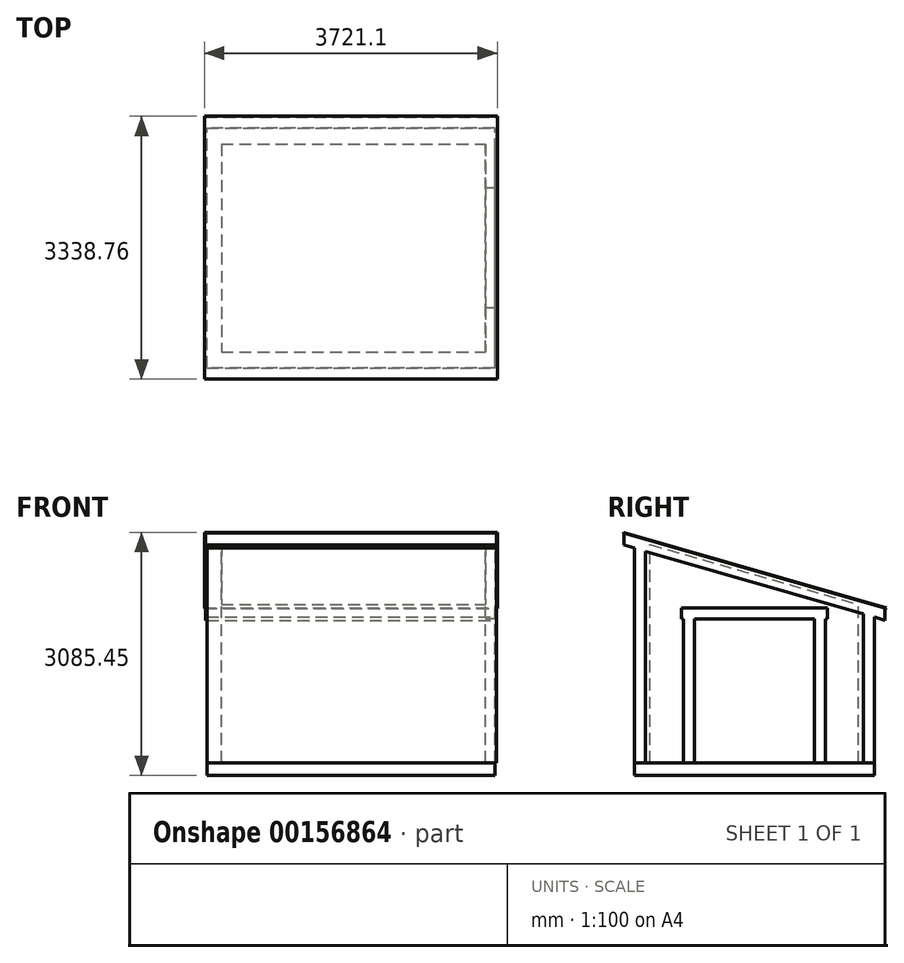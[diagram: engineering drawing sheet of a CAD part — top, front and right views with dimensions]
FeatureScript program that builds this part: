
annotation { "Feature Type Name" : "Feature", "Feature Type Description" : "" }
export const myFeature = defineFeature(function(context is Context, id is Id, definition is map)
    precondition{}
    {
        {
            var Q0;
            Q0=qCreatedBy(makeId("Top.planeOp"),FACE);
            var sketch = newSketch(context, id + "F0", { "sketchPlane" : qUnion([Q0])});
            skLineSegment(sketch, "E0.bottom", {"start": v(-3657.6, 0) * mm, "end": v(0, 0) * mm});
            skLineSegment(sketch, "E0.top", {"start": v(-3657.6, 3048) * mm, "end": v(0, 3048) * mm});
            skLineSegment(sketch, "E0.left", {"start": v(0, 0) * mm, "end": v(0, 3048) * mm});
            skLineSegment(sketch, "E0.right", {"start": v(-3657.6, 0) * mm, "end": v(-3657.6, 3048) * mm});
            skSolve(sketch);
        }
        {
            var Q0;
            Q0=makeQuery(id+"F0.imprint","IMPRINT",FACE,{"disambiguationData":[TD([[makeQuery(id+"F0.imprint","IMPRINT",EDGE,{"derivedFrom":sQuery(id+"F0.wireOp",EDGE,"E0.bottom")}),1.0]])]});
            extrude(context, id + "F1", {"entities" : qUnion([Q0]), "depth" : 2880.36 * mm});
        }
        {
            var Q0;
            Q0=makeQuery(id+"F1.opExtrude","CAP_EDGE",EDGE,{"disambiguationData":[OSD([sQuery(id+"F0.wireOp",EDGE,"E0.top")])],"isStart":false});
            chamfer(context, id + "F2", {"entities" : qUnion([Q0]), "chamferType" : ChamferType.TWO_OFFSETS, "width1" : 876.3 * mm, "oppositeDirection" : false, "width2" : 3048 * mm, "tangentPropagation" : true});
        }
        {
            var Q0;
            Q0=makeQuery(id+"F2.opChamfer","BLEND_FACE",FACE,{"disambiguationData":[OSD([sQuery(id+"F0.wireOp",EDGE,"E0.top")])]});
            var sketch = newSketch(context, id + "F3", { "sketchPlane" : qUnion([Q0])});
            skLineSegment(sketch, "E1.1", {"start": v(-3676.65, -937.33) * mm, "end": v(-3676.65, 2517.07) * mm});
            skLineSegment(sketch, "E1.3", {"start": v(19.05, 2517.07) * mm, "end": v(19.05, -937.33) * mm});
            skLineSegment(sketch, "E2", {"start": v(19.05, 789.87) * mm, "end": v(0, 789.87) * mm, "construction": true});
            skLineSegment(sketch, "E3", {"start": v(0, 789.87) * mm, "end": v(-3657.6, 789.87) * mm, "construction": true});
            skLineSegment(sketch, "E4.0", {"start": v(-3657.6, -795.86) * mm, "end": v(-3657.6, 743.55) * mm, "construction": true});
            skLineSegment(sketch, "E5", {"start": v(-3657.6, 789.87) * mm, "end": v(-3657.6, 2375.6) * mm, "construction": true});
            skLineSegment(sketch, "E6", {"start": v(-3657.6, 743.55) * mm, "end": v(-3657.6, 789.87) * mm, "construction": true});
            skLineSegment(sketch, "E7", {"start": v(-3657.6, 789.87) * mm, "end": v(-3676.65, 789.87) * mm, "construction": true});
            skLineSegment(sketch, "E8", {"start": v(19.05, -937.33) * mm, "end": v(-3676.65, -937.33) * mm});
            skLineSegment(sketch, "E9", {"start": v(-3676.65, 2517.07) * mm, "end": v(19.05, 2517.07) * mm});
            skLineSegment(sketch, "E10.0", {"start": v(-3657.6, -795.86) * mm, "end": v(0, -795.86) * mm, "construction": true});
            skLineSegment(sketch, "E10.1", {"start": v(0, 2375.6) * mm, "end": v(0, -795.86) * mm, "construction": true});
            skSolve(sketch);
        }
        {
            var Q0;
            Q0=makeQuery(id+"F1.opExtrude","SWEPT_FACE",FACE,{"disambiguationData":[OSD([sQuery(id+"F0.wireOp",EDGE,"E0.left")])]});
            var sketch = newSketch(context, id + "F4", { "sketchPlane" : qUnion([Q0])});
            skLineSegment(sketch, "E11.0", {"start": v(0, 2880.36) * mm, "end": v(0, 0) * mm, "construction": true});
            skLineSegment(sketch, "E12", {"start": v(0, 2880.36) * mm, "end": v(0, 2727.96) * mm});
            skSolve(sketch);
        }
        {
            var Q0;
            Q0=makeQuery(id+"F3.imprint","IMPRINT",FACE,{"disambiguationData":[TD([[makeQuery(id+"F3.imprint","IMPRINT",EDGE,{"derivedFrom":sQuery(id+"F3.wireOp",EDGE,"E1.1")}),-1.0]])]});
            var Q1;
            Q1=sQuery(id+"F4.wireOp",EDGE,"E12");
            sweep(context, id + "F5", {"operationType" : NewBodyOperationType.ADD, "profiles" : qUnion([Q0]), "path" : qUnion([Q1])});
        }
        {
            var Q0;
            {var subQ0=sQuery(id+"F0.wireOp",EDGE,"E0.top");Q0=makeQuery(id+"F5.boolean.opBoolean","MERGE",FACE,{"derivedFrom":[makeQuery(id+"F2.opChamfer","BLEND_FACE",FACE,{"disambiguationData":[OSD([subQ0])]}),makeQuery(id+"F5.opSweep","CAP_FACE",FACE,{"disambiguationData":[OSD([sQuery(id+"F0.wireOp",EDGE,"E0.bottom"),subQ0,sQuery(id+"F0.wireOp",EDGE,"E0.left"),sQuery(id+"F0.wireOp",EDGE,"E0.right"),sQuery(id+"F3.wireOp",EDGE,"E1.1"),sQuery(id+"F3.wireOp",EDGE,"E1.3"),sQuery(id+"F3.wireOp",EDGE,"E8"),sQuery(id+"F3.wireOp",EDGE,"E9"),sQuery(id+"F4.wireOp",VERTEX,"E12.start")])],"isStart":true})]});}
            var sketch = newSketch(context, id + "F6", { "sketchPlane" : qUnion([Q0])});
            skLineSegment(sketch, "E13.0", {"start": v(19.05, -937.33) * mm, "end": v(-3676.65, -937.33) * mm, "construction": true});
            skLineSegment(sketch, "E13.1", {"start": v(19.05, 2517.07) * mm, "end": v(19.05, -937.33) * mm, "construction": true});
            skLineSegment(sketch, "E13.2", {"start": v(-3676.65, 2517.07) * mm, "end": v(19.05, 2517.07) * mm, "construction": true});
            skLineSegment(sketch, "E13.3", {"start": v(-3676.65, -895.22) * mm, "end": v(-3676.65, 2559.18) * mm, "construction": true});
            skLineSegment(sketch, "E14", {"start": v(31.75, -942.41) * mm, "end": v(-3689.35, -942.41) * mm});
            skLineSegment(sketch, "E15", {"start": v(-3689.35, -942.41) * mm, "end": v(-3689.35, 2529.77) * mm});
            skLineSegment(sketch, "E16", {"start": v(-3689.35, 2529.77) * mm, "end": v(31.75, 2529.77) * mm});
            skLineSegment(sketch, "E17", {"start": v(31.75, 2529.77) * mm, "end": v(31.75, -942.41) * mm});
            skLineSegment(sketch, "E18", {"start": v(-461.3, -942.41) * mm, "end": v(-461.3, -937.33) * mm, "construction": true});
            skLineSegment(sketch, "E19", {"start": v(-683.5, 2517.07) * mm, "end": v(-683.5, 2529.77) * mm, "construction": true});
            skLineSegment(sketch, "E20", {"start": v(31.75, 1297.2) * mm, "end": v(19.05, 1297.2) * mm, "construction": true});
            skLineSegment(sketch, "E21", {"start": v(-3676.65, 831.98) * mm, "end": v(-3689.35, 831.98) * mm, "construction": true});
            skPoint(sketch, "E21.endSnap0", {"position": v(-3689.35, 793.68) * mm});
            skSolve(sketch);
        }
        {
            var Q0;
            Q0 = qSketchRegion(id + "F6", true);
            extrude(context, id + "F7", {"entities" : qUnion([Q0]), "operationType" : NewBodyOperationType.ADD, "depth" : 6.35 * mm});
        }
        {
            var Q0;
            Q0=makeQuery(id+"F1.opExtrude","SWEPT_FACE",FACE,{"disambiguationData":[OSD([sQuery(id+"F0.wireOp",EDGE,"E0.left")])]});
            var sketch = newSketch(context, id + "F8", { "sketchPlane" : qUnion([Q0])});
            skLineSegment(sketch, "E22.top", {"start": v(0, 0) * mm, "end": v(139.7, 0) * mm});
            skLineSegment(sketch, "E22.left", {"start": v(0, 2727.96) * mm, "end": v(0, 0) * mm});
            skLineSegment(sketch, "E22.right", {"start": v(139.7, 2687.8) * mm, "end": v(139.7, 0) * mm});
            skLineSegment(sketch, "E23", {"start": v(0, 2727.96) * mm, "end": v(139.7, 2687.8) * mm});
            skLineSegment(sketch, "E24.bottom", {"start": v(3048, 0) * mm, "end": v(2908.3, 0) * mm});
            skLineSegment(sketch, "E24.left", {"start": v(3048, 0) * mm, "end": v(3048, 1851.66) * mm});
            skLineSegment(sketch, "E24.right", {"start": v(2908.3, 0) * mm, "end": v(2908.3, 1891.82) * mm});
            skLineSegment(sketch, "E25", {"start": v(2908.3, 1891.82) * mm, "end": v(3048, 1851.66) * mm});
            skLineSegment(sketch, "E26", {"start": v(139.7, 0) * mm, "end": v(2908.3, 0) * mm, "construction": true});
            skLineSegment(sketch, "E27.bottom", {"start": v(2286, 1828.8) * mm, "end": v(762, 1828.8) * mm, "construction": true});
            skLineSegment(sketch, "E27.left", {"start": v(2286, 1828.8) * mm, "end": v(2286, 0) * mm, "construction": true});
            skLineSegment(sketch, "E27.right", {"start": v(762, 1828.8) * mm, "end": v(762, 0) * mm, "construction": true});
            skPoint(sketch, "E27.middle", {"position": v(1524, 0) * mm});
            skPoint(sketch, "E28", {"position": v(1524, 1828.8) * mm});
            skLineSegment(sketch, "E29", {"start": v(1524, 1828.8) * mm, "end": v(1524, 0) * mm, "construction": true});
            skLineSegment(sketch, "E30.bottom", {"start": v(762, 0) * mm, "end": v(622.3, 0) * mm});
            skLineSegment(sketch, "E30.top", {"start": v(762, 1828.8) * mm, "end": v(622.3, 1828.8) * mm});
            skLineSegment(sketch, "E30.left", {"start": v(762, 0) * mm, "end": v(762, 1828.8) * mm});
            skLineSegment(sketch, "E30.right", {"start": v(622.3, 0) * mm, "end": v(622.3, 1828.8) * mm});
            skLineSegment(sketch, "E31.MirrorCS", {"start": v(2425.7, 0) * mm, "end": v(2425.7, 1828.8) * mm});
            skLineSegment(sketch, "E32.MirrorCS", {"start": v(2286, 1828.8) * mm, "end": v(2425.7, 1828.8) * mm});
            skLineSegment(sketch, "E33.MirrorCS", {"start": v(2908.3, 0) * mm, "end": v(139.7, 0) * mm, "construction": true});
            skLineSegment(sketch, "E34", {"start": v(2286, 1828.8) * mm, "end": v(2286, 0) * mm});
            skLineSegment(sketch, "E35", {"start": v(1524, 1828.8) * mm, "end": v(2451.1, 1828.8) * mm});
            skLineSegment(sketch, "E36", {"start": v(2451.1, 1828.8) * mm, "end": v(2451.1, 1968.5) * mm});
            skLineSegment(sketch, "E37", {"start": v(2451.1, 1968.5) * mm, "end": v(1524, 1968.5) * mm});
            skLineSegment(sketch, "E38.MirrorCS", {"start": v(596.9, 1968.5) * mm, "end": v(1524, 1968.5) * mm});
            skLineSegment(sketch, "E39.MirrorCS", {"start": v(596.9, 1828.8) * mm, "end": v(596.9, 1968.5) * mm});
            skLineSegment(sketch, "E40.MirrorCS", {"start": v(1524, 1828.8) * mm, "end": v(596.9, 1828.8) * mm});
            skLineSegment(sketch, "E41", {"start": v(2286, 0) * mm, "end": v(2425.7, 0) * mm});
            skSolve(sketch);
        }
        {
            var Q0;
            Q0 = qSketchRegion(id + "F8", true);
            extrude(context, id + "F9", {"entities" : qUnion([Q0]), "operationType" : NewBodyOperationType.ADD, "depth" : 19.05 * mm});
        }
        {
            var Q0;
            {var subQ0=sQuery(id+"F0.wireOp",EDGE,"E0.left");Q0=makeQuery(id+"F9.boolean.opBoolean","SPLIT",FACE,{"disambiguationData":[TD([makeQuery(id+"F9.opExtrude","SWEPT_FACE",FACE,{"disambiguationData":[OSD([sQuery(id+"F8.wireOp",EDGE,"E30.left")])]})])],"derivedFrom":makeQuery(id+"F1.opExtrude","SWEPT_FACE",FACE,{"disambiguationData":[OSD([subQ0])]})});}
            extrude(context, id + "F10", {"entities" : qUnion([Q0]), "operationType" : NewBodyOperationType.REMOVE, "oppositeDirection" : true, "depth" : 121.92 * mm});
        }
        {
            var Q0;
            Q0=makeQuery(id+"F10.boolean.opBoolean","COPY",FACE,{"derivedFrom":makeQuery(id+"F10.opExtrude","CAP_FACE",FACE,{"disambiguationData":[OSD([sQuery(id+"F0.wireOp",EDGE,"E0.left")])],"isStart":false})});
            var sketch = newSketch(context, id + "F11", { "sketchPlane" : qUnion([Q0])});
            skLineSegment(sketch, "E42.bottom", {"start": v(2843.33, 0) * mm, "end": v(198.9, 0) * mm});
            skLineSegment(sketch, "E42.left", {"start": v(2843.33, 0) * mm, "end": v(2843.33, 2012.4) * mm});
            skLineSegment(sketch, "E42.right", {"start": v(198.9, 0) * mm, "end": v(198.9, 2772.67) * mm});
            skLineSegment(sketch, "E43", {"start": v(198.9, 2772.67) * mm, "end": v(2843.33, 2012.4) * mm});
            skSolve(sketch);
        }
        {
            var Q0;
            Q0 = qSketchRegion(id + "F11", true);
            extrude(context, id + "F12", {"entities" : qUnion([Q0]), "operationType" : NewBodyOperationType.REMOVE, "oppositeDirection" : true, "depth" : 3352.8 * mm});
        }
        {
            var Q0;
            Q0=qCreatedBy(makeId("Top.planeOp"),FACE);
            var sketch = newSketch(context, id + "F13", { "sketchPlane" : qUnion([Q0])});
            skLineSegment(sketch, "E44.bottom", {"start": v(0, 0) * mm, "end": v(-3657.6, 0) * mm});
            skLineSegment(sketch, "E44.top", {"start": v(0, 3048) * mm, "end": v(-3657.6, 3048) * mm});
            skLineSegment(sketch, "E44.left", {"start": v(0, 0) * mm, "end": v(0, 3048) * mm});
            skLineSegment(sketch, "E44.right", {"start": v(-3657.6, 0) * mm, "end": v(-3657.6, 3048) * mm});
            skPoint(sketch, "E45.0", {"position": v(-3657.6, 3048) * mm});
            skSolve(sketch);
        }
        {
            var Q0;
            Q0 = qSketchRegion(id + "F13", true);
            extrude(context, id + "F14", {"entities" : qUnion([Q0]), "oppositeDirection" : true, "depth" : 158.5 * mm});
        }
        {
            var Q0;
            Q0=makeQuery(id+"F14.opExtrude","CAP_FACE",FACE,{"disambiguationData":[OSD([sQuery(id+"F13.wireOp",EDGE,"E44.bottom"),sQuery(id+"F13.wireOp",EDGE,"E44.top"),sQuery(id+"F13.wireOp",EDGE,"E44.left"),sQuery(id+"F13.wireOp",EDGE,"E44.right")])],"isStart":false});
            cPlane(context, id + "F15", {"entities" : qUnion([Q0]), "cplaneType" : CPlaneType.OFFSET, "offset" : 25.4 * mm, "width" : 152.4 * mm, "height" : 152.4 * mm});
        }
        {
            var Q0;
            Q0=makeQuery(id+"F9.boolean.opBoolean","MERGE",FACE,{"derivedFrom":[makeQuery(id+"F5.opSweep","SWEPT_FACE",FACE,{"disambiguationData":[OSD([sQuery(id+"F3.wireOp",EDGE,"E1.3"),sQuery(id+"F4.wireOp",EDGE,"E12")])]}),makeQuery(id+"F9.opExtrude","CAP_FACE",FACE,{"disambiguationData":[OSD([sQuery(id+"F8.wireOp",EDGE,"E22.top"),sQuery(id+"F8.wireOp",EDGE,"E22.left"),sQuery(id+"F8.wireOp",EDGE,"E22.right"),sQuery(id+"F8.wireOp",EDGE,"E23")])],"isStart":false}),makeQuery(id+"F9.opExtrude","CAP_FACE",FACE,{"disambiguationData":[OSD([sQuery(id+"F8.wireOp",EDGE,"E24.bottom"),sQuery(id+"F8.wireOp",EDGE,"E24.left"),sQuery(id+"F8.wireOp",EDGE,"E24.right"),sQuery(id+"F8.wireOp",EDGE,"E25")])],"isStart":false})]});
            var sketch = newSketch(context, id + "F16", { "sketchPlane" : qUnion([Q0])});
            skLineSegment(sketch, "E46", {"start": v(0, 2171.7) * mm, "end": v(2464.9, 2171.7) * mm, "construction": true});
            skLineSegment(sketch, "E47.0", {"start": v(2286, 1828.8) * mm, "end": v(762, 1828.8) * mm, "construction": true});
            skSolve(sketch);
        }
        {
            var Q0;
            Q0=sQuery(id+"F16.wireOp",EDGE,"E46");
            cPlane(context, id + "F17", {"entities" : qUnion([Q0]), "cplaneType" : CPlaneType.LINE_ANGLE, "offset" : 25.4 * mm, "angle" : 5.71 * degree, "width" : 152.4 * mm, "height" : 152.4 * mm});
        }
    });
